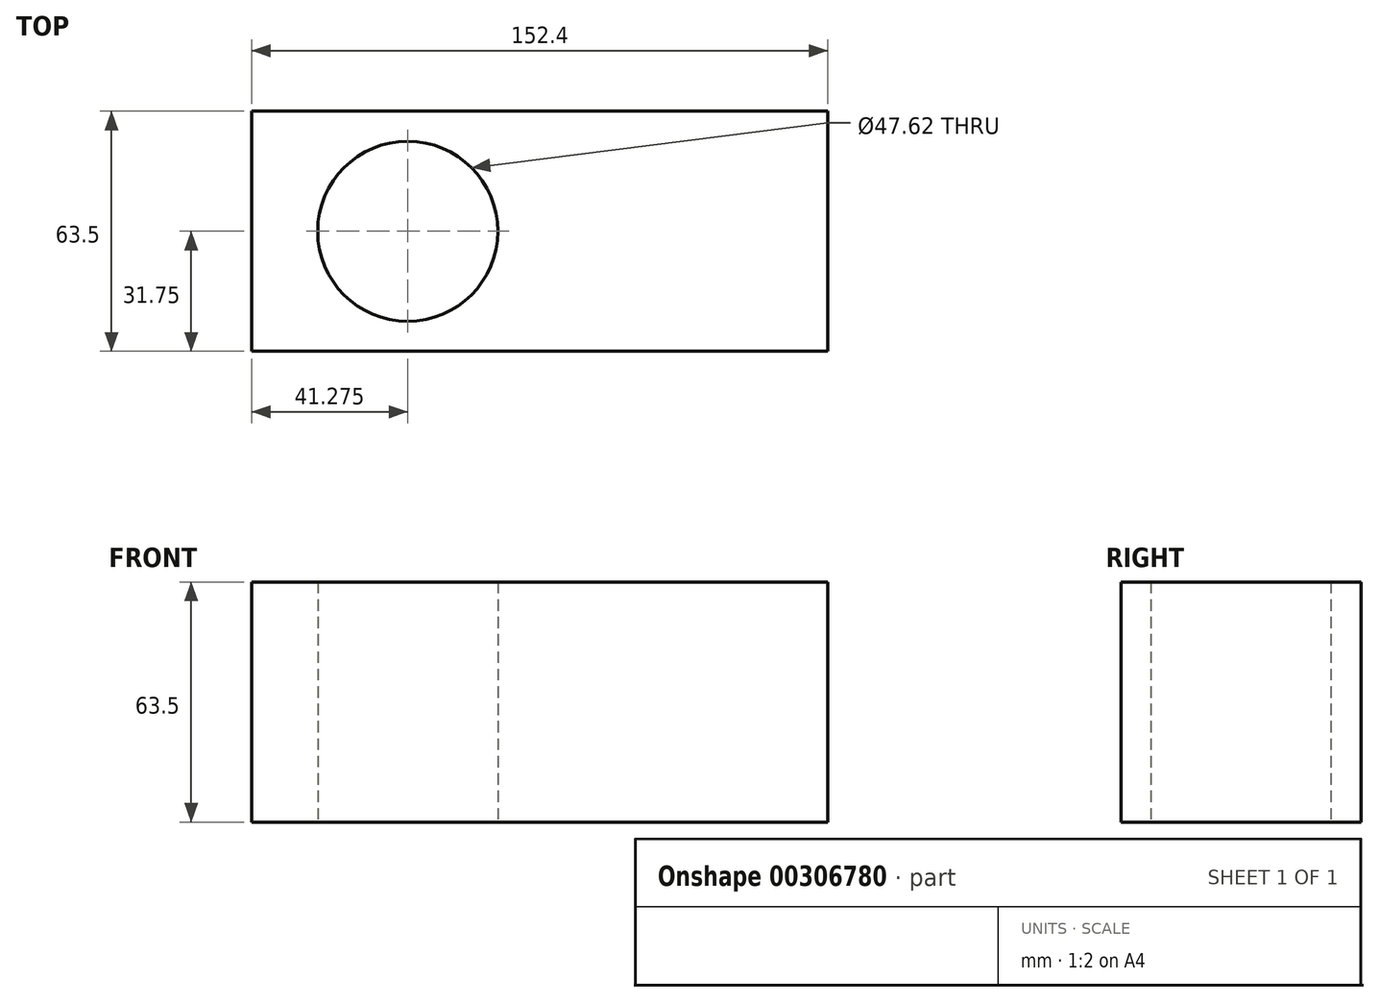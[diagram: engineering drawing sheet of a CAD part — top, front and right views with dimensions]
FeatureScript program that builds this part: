
annotation { "Feature Type Name" : "Feature", "Feature Type Description" : "" }
export const myFeature = defineFeature(function(context is Context, id is Id, definition is map)
    precondition{}
    {
        {
            var Q0;
            Q0=qCreatedBy(makeId("Right.planeOp"),FACE);
            var sketch = newSketch(context, id + "F0", { "sketchPlane" : qUnion([Q0])});
            skLineSegment(sketch, "E0", {"start": v(-31.75, -31.75) * mm, "end": v(-31.75, 31.75) * mm});
            skLineSegment(sketch, "E1", {"start": v(-31.75, 31.75) * mm, "end": v(31.75, 31.75) * mm});
            skLineSegment(sketch, "E2", {"start": v(31.75, 31.75) * mm, "end": v(31.75, -31.75) * mm});
            skLineSegment(sketch, "E3", {"start": v(31.75, -31.75) * mm, "end": v(-31.75, -31.75) * mm});
            skSolve(sketch);
        }
        {
            var Q0;
            Q0=makeQuery(id+"F0.imprint","IMPRINT",FACE,{"disambiguationData":[TD([[makeQuery(id+"F0.imprint","IMPRINT",EDGE,{"derivedFrom":sQuery(id+"F0.wireOp",EDGE,"E0")}),-1.0]])]});
            extrude(context, id + "F1", {"entities" : qUnion([Q0]), "depth" : 152.4 * mm, "symmetric" : true});
        }
        {
            var Q0;
            Q0=makeQuery(id+"F1.opExtrude","SWEPT_FACE",FACE,{"disambiguationData":[OSD([sQuery(id+"F0.wireOp",EDGE,"E1")])]});
            var sketch = newSketch(context, id + "F2", { "sketchPlane" : qUnion([Q0])});
            skPoint(sketch, "E4", {"position": v(-34.92, 0) * mm});
            skSolve(sketch);
        }
        {
            var Q0;
            Q0=sQuery(id+"F2.wireOp",VERTEX,"E4");
            var Q1;
            Q1=makeQuery(id+"F1.opExtrude","SWEPT_BODY",BODY,{"disambiguationData":[OSD([sQuery(id+"F0.wireOp",EDGE,"E0"),sQuery(id+"F0.wireOp",EDGE,"E1"),sQuery(id+"F0.wireOp",EDGE,"E2"),sQuery(id+"F0.wireOp",EDGE,"E3")])]});
            hole(context, id + "F3", {"style" : HoleStyle.SIMPLE, "endStyle" : HoleEndStyle.THROUGH, "holeDiameter" : 47.62 * mm, "tappedDepth" : 12.7 * mm, "tapClearance" : 3, "locations" : qUnion([Q0]), "scope" : qUnion([Q1]), "startStyle" : HoleStartStyle.PART});
        }
    });
